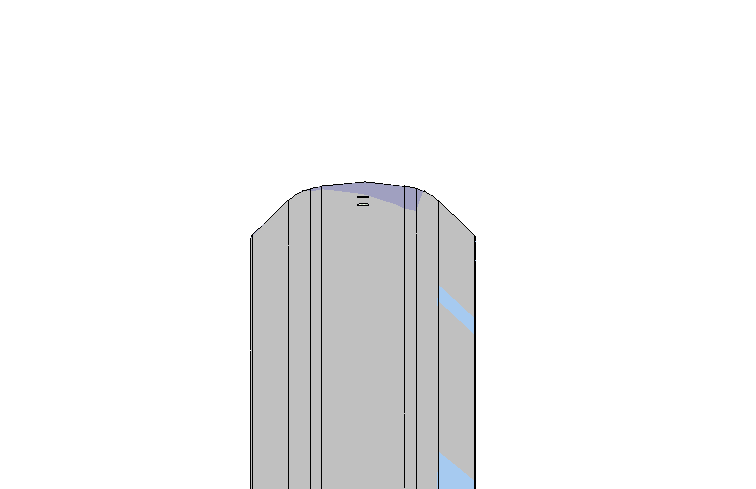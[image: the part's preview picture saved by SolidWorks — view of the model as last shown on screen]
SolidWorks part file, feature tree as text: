
SOLIDWORKS PART (.sldprt)
format: sldprt  version: not decoded by parser v0  size: 573,440 bytes
history: native  units: mm
features: plane x5, sketch x4, cut_revolve x2, material x1, revolve x1, cut_extrude x1 (+10 scaffold rows collapsed)
feature tree (24):
  scaffold x10  (default folders/planes/origin — collapsed)
  material  "Matériau <non spécifié>"
  plane  "Plan de face"
  plane  "Plan de dessus"
  plane  "Plan de droite"
  sketch  "Esquisse1"  dims[c1.D5=0.1mm c1.D3=1.6mm c1.D8=~3.336064mm c1.D10=0.1mm c1.D4=50.0mm c2.D5=51.5mm c2.D6=10.0mm c2.D13=11.5mm c2.D8=1.6mm c2.D1=21.0mm c2.D2=33.0mm c2.D3=58.0mm c3.D6=2.5mm c3.D3=21.0mm c3.D7=33.0mm c3.D8=59.0mm c3.D11=3.0mm c3.D12=0.05mm c3.D2=370.0mm c3.D5=17.0mm c4.D8=59.0mm c4.D14=~338.322242mm c4.D4=1.5mm c4.D9=1.5mm]
  revolve  "Révolution1"  Angle=88deg
  plane  "Plan1"  Offset=136.75mm
  plane  "Plan2"  Offset=125mm
  sketch  "Esquisse2"  dims[c1.D1=~9.350811mm c2.D1=35.0deg]
  cut_extrude  "Enlèv. mat.-Extru.1"  [1 undecoded]
  sketch  "Esquisse4"  dims[c1.D1=~68.515563mm c2.D1=8.7deg c2.D3=~74.603227mm c3.D1=~487.53427mm c4.D1=8.97deg c4.D2=1.5mm]
  cut_revolve  "Enlèvement de matière-Révolution1"  Angle=360deg
  sketch  "Esquisse5"  dims[c1.D1=~403.135217mm c2.D1=1.8deg c2.D2=3.0mm]
  cut_revolve  "Enlèvement de matière-Révolution2"  Angle=360deg
decode coverage: 7 of 8 modeling features carry decoded parameters
note: ~ marks probable driven/reference dimensions
note: 1 parameter value undecoded
note: suppression state not decoded; provenance and decode notes live in map.json
